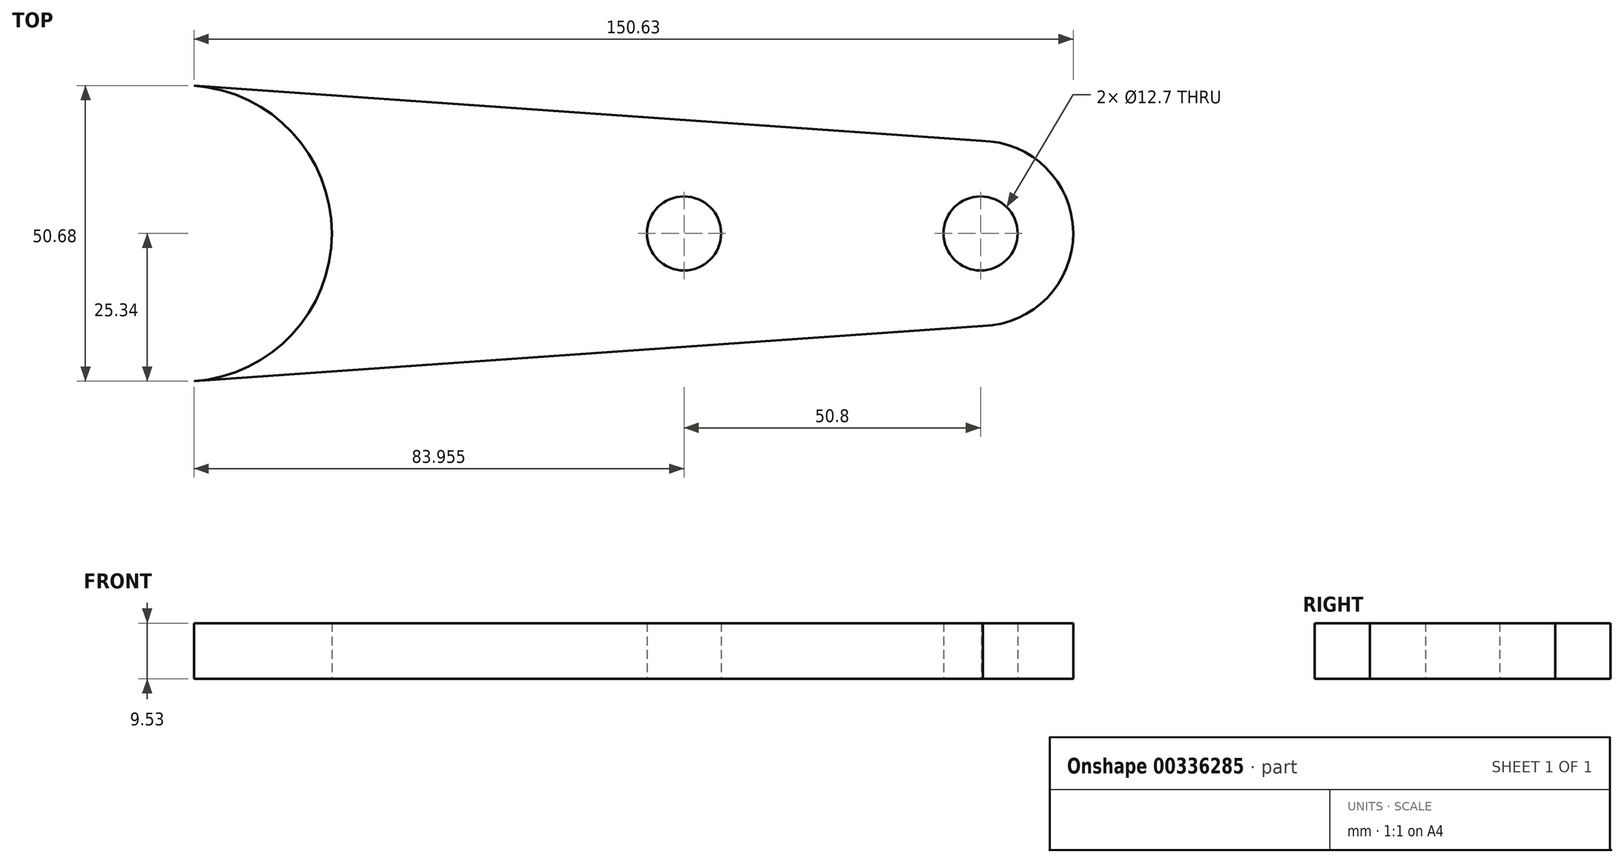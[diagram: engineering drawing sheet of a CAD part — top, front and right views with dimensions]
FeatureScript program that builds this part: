
annotation { "Feature Type Name" : "Feature", "Feature Type Description" : "" }
export const myFeature = defineFeature(function(context is Context, id is Id, definition is map)
    precondition{}
    {
        {
            var Q0;
            Q0=qCreatedBy(makeId("Top.planeOp"),FACE);
            var sketch = newSketch(context, id + "F0", { "sketchPlane" : qUnion([Q0])});
            skArc(sketch, "E0", {"start": v(1.77, -25.34) * mm, "mid": v(25.4, 0) * mm, "end": v(1.78, 25.34) * mm});
            skCircle(sketch, "E1", {"center": v(85.73, 0) * mm, "radius": 6.35 * mm});
            skCircle(sketch, "E2", {"center": v(136.53, 0) * mm, "radius": 6.35 * mm});
            skArc(sketch, "E3", {"start": v(136.93, -15.87) * mm, "mid": v(152.4, 0.14) * mm, "end": v(136.64, 15.87) * mm});
            skLineSegment(sketch, "E4", {"start": v(136.93, -15.87) * mm, "end": v(1.77, -25.34) * mm});
            skLineSegment(sketch, "E5", {"start": v(136.64, 15.87) * mm, "end": v(1.78, 25.34) * mm});
            skSolve(sketch);
        }
        {
            var Q0;
            Q0 = qSketchRegion(id + "F0", true);
            extrude(context, id + "F1", {"entities" : qUnion([Q0]), "depth" : 9.52 * mm});
        }
    });
